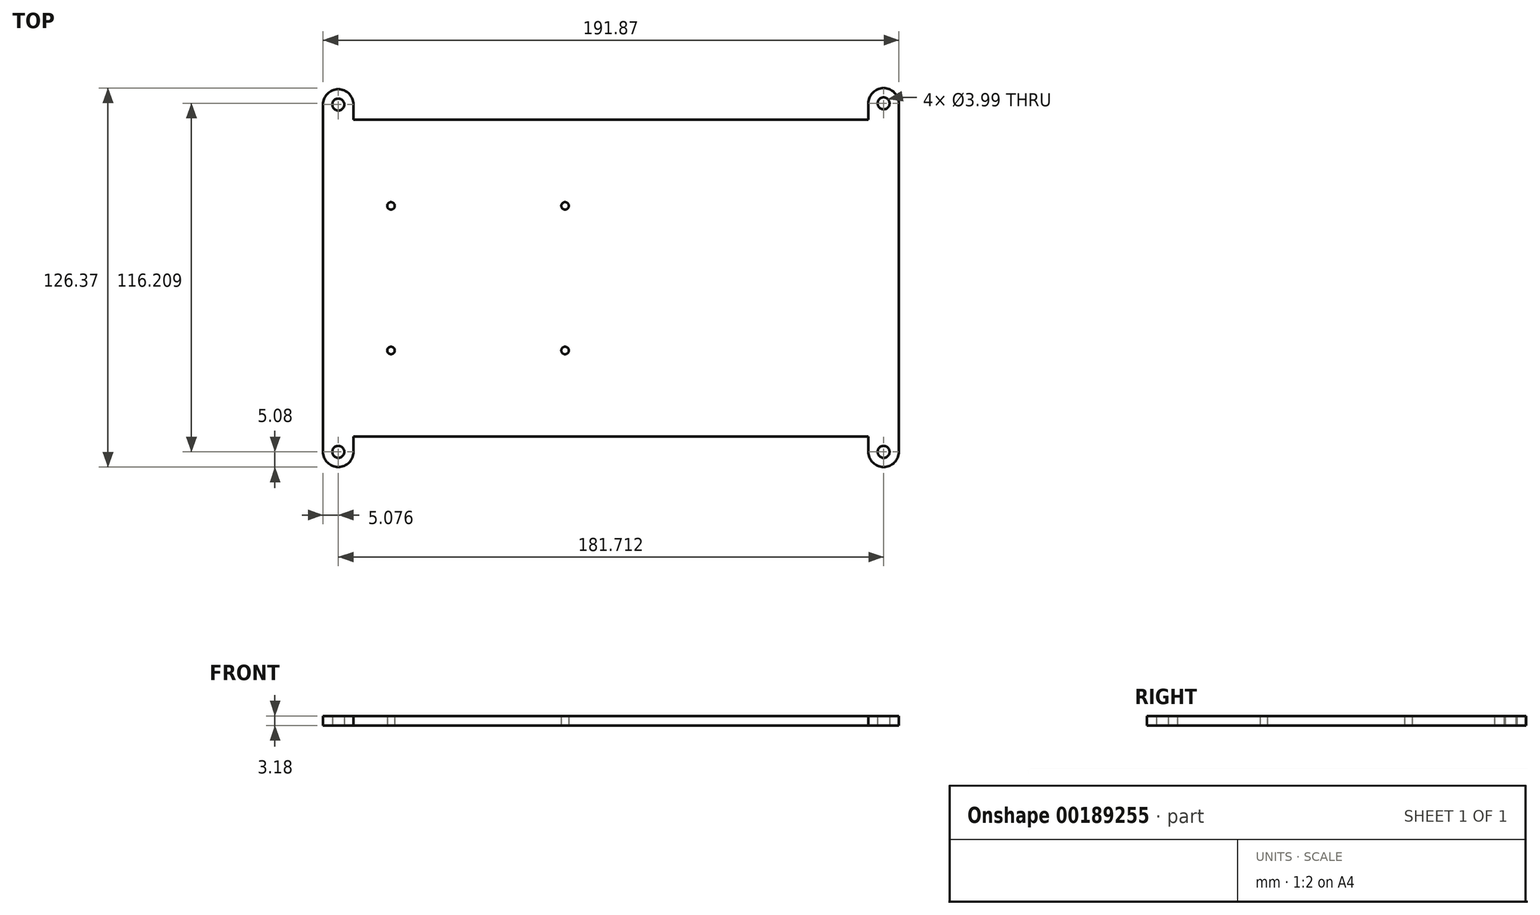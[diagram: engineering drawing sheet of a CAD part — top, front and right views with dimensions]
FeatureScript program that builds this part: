
annotation { "Feature Type Name" : "Feature", "Feature Type Description" : "" }
export const myFeature = defineFeature(function(context is Context, id is Id, definition is map)
    precondition{}
    {
        {
            var Q0;
            Q0=qCreatedBy(makeId("Top.planeOp"),FACE);
            var sketch = newSketch(context, id + "F0", { "sketchPlane" : qUnion([Q0])});
            skLineSegment(sketch, "E0", {"start": v(165.77, 105.66) * mm, "end": v(337.32, 105.66) * mm});
            skLineSegment(sketch, "E1", {"start": v(165.77, 0) * mm, "end": v(337.32, 0) * mm});
            skLineSegment(sketch, "E2", {"start": v(155.6, 110.74) * mm, "end": v(155.6, -5.08) * mm});
            skLineSegment(sketch, "E3", {"start": v(337.32, 0) * mm, "end": v(337.32, -5.08) * mm});
            skLineSegment(sketch, "E4", {"start": v(337.32, 105.66) * mm, "end": v(337.32, 111.13) * mm});
            skLineSegment(sketch, "E5", {"start": v(347.48, 111.13) * mm, "end": v(347.48, -5.08) * mm});
            skArc(sketch, "E6", {"start": v(337.32, -5.08) * mm, "mid": v(342.4, -10.16) * mm, "end": v(347.48, -5.08) * mm});
            skArc(sketch, "E7", {"start": v(337.32, 111.13) * mm, "mid": v(342.4, 116.2) * mm, "end": v(347.48, 111.13) * mm});
            skCircle(sketch, "E8", {"center": v(342.4, -5.08) * mm, "radius": 2 * mm});
            skCircle(sketch, "E9", {"center": v(342.4, 111.13) * mm, "radius": 2 * mm});
            skPoint(sketch, "E10", {"position": v(236.24, 52.83) * mm});
            skLineSegment(sketch, "E11", {"start": v(165.77, 105.66) * mm, "end": v(165.77, 110.74) * mm});
            skLineSegment(sketch, "E12", {"start": v(165.77, 0) * mm, "end": v(165.77, -5.08) * mm});
            skArc(sketch, "E13", {"start": v(155.6, 110.74) * mm, "mid": v(160.69, 115.82) * mm, "end": v(165.77, 110.74) * mm});
            skArc(sketch, "E14", {"start": v(155.6, -5.08) * mm, "mid": v(160.69, -10.16) * mm, "end": v(165.77, -5.08) * mm});
            skCircle(sketch, "E15", {"center": v(160.69, -5.08) * mm, "radius": 2 * mm});
            skCircle(sketch, "E16", {"center": v(160.69, 110.74) * mm, "radius": 2 * mm});
            skCircle(sketch, "E17", {"center": v(178.24, 76.95) * mm, "radius": 1.25 * mm});
            skCircle(sketch, "E18", {"center": v(178.24, 28.72) * mm, "radius": 1.25 * mm});
            skCircle(sketch, "E19", {"center": v(236.24, 28.72) * mm, "radius": 1.25 * mm});
            skCircle(sketch, "E20", {"center": v(236.24, 76.95) * mm, "radius": 1.25 * mm});
            skSolve(sketch);
        }
        {
            var Q0;
            Q0=makeQuery(id+"F0.imprint","IMPRINT",FACE,{"disambiguationData":[TD([[makeQuery(id+"F0.imprint","IMPRINT",EDGE,{"derivedFrom":sQuery(id+"F0.wireOp",EDGE,"E0")}),-1.0]])]});
            extrude(context, id + "F1", {"entities" : qUnion([Q0]), "depth" : 3.17 * mm});
        }
    });
